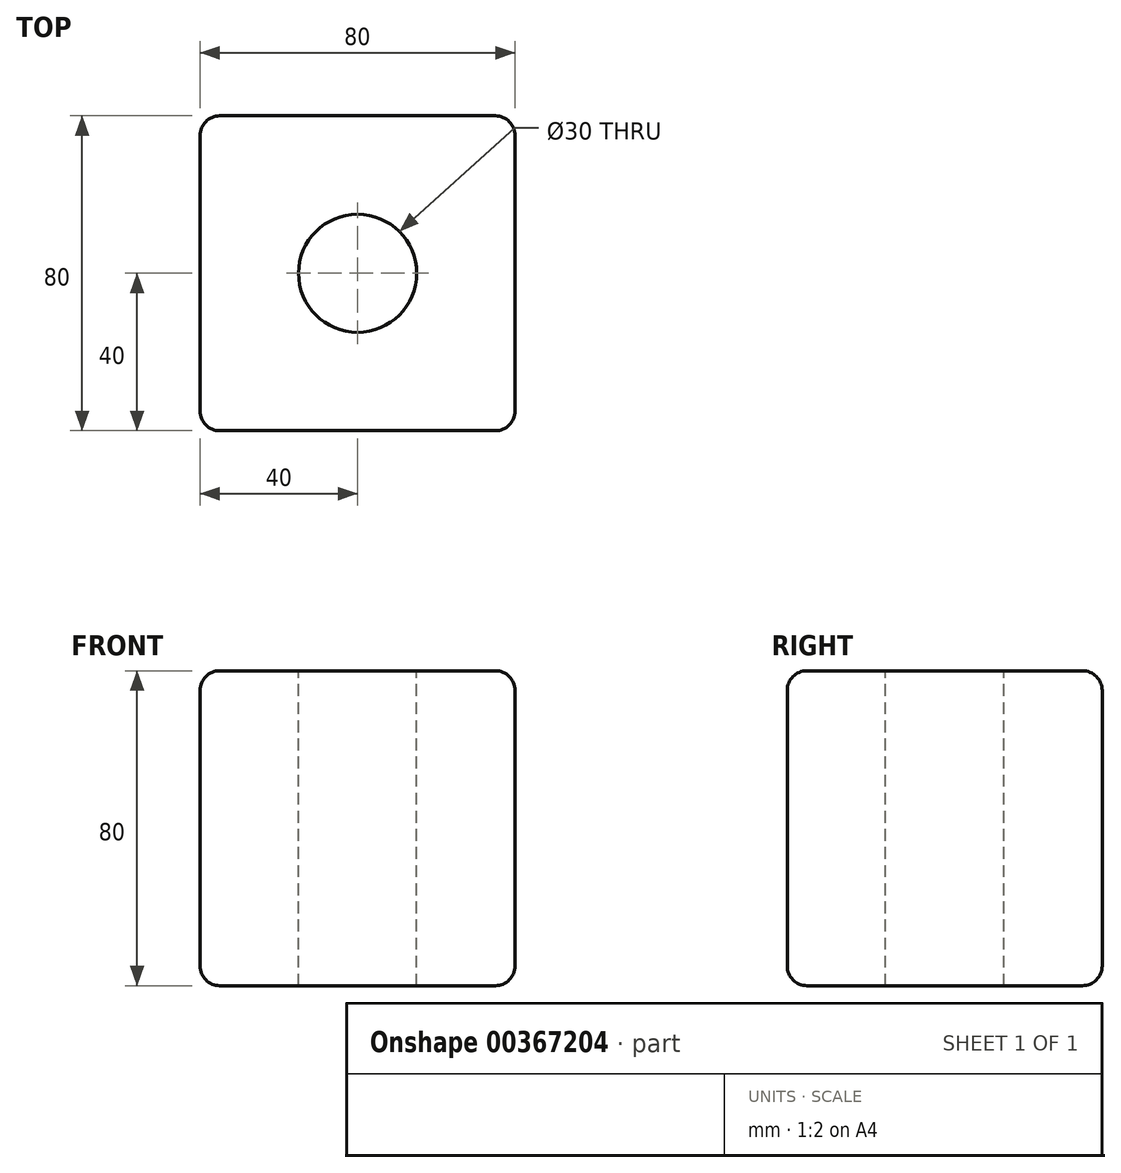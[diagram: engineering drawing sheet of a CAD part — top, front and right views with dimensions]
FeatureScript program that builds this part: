
annotation { "Feature Type Name" : "Feature", "Feature Type Description" : "" }
export const myFeature = defineFeature(function(context is Context, id is Id, definition is map)
    precondition{}
    {
        {
            var Q0;
            Q0=qCreatedBy(makeId("Top.planeOp"),FACE);
            var sketch = newSketch(context, id + "F0", { "sketchPlane" : qUnion([Q0])});
            skLineSegment(sketch, "E0.bottom", {"start": v(-40, 40) * mm, "end": v(40, 40) * mm});
            skLineSegment(sketch, "E0.top", {"start": v(-40, -40) * mm, "end": v(40, -40) * mm});
            skLineSegment(sketch, "E0.left", {"start": v(-40, 40) * mm, "end": v(-40, -40) * mm});
            skLineSegment(sketch, "E0.right", {"start": v(40, 40) * mm, "end": v(40, -40) * mm});
            skPoint(sketch, "E0.middle", {"position": v(0, 0) * mm});
            skSolve(sketch);
        }
        {
            var Q0;
            Q0=makeQuery(id+"F0.imprint","IMPRINT",FACE,{"disambiguationData":[TD([[makeQuery(id+"F0.imprint","IMPRINT",EDGE,{"derivedFrom":sQuery(id+"F0.wireOp",EDGE,"E0.bottom")}),-1.0]])]});
            extrude(context, id + "F1", {"entities" : qUnion([Q0]), "depth" : 80 * mm});
        }
        {
            var Q0;
            Q0=makeQuery(id+"F1.opExtrude","CAP_FACE",FACE,{"disambiguationData":[OSD([sQuery(id+"F0.wireOp",EDGE,"E0.bottom"),sQuery(id+"F0.wireOp",EDGE,"E0.top"),sQuery(id+"F0.wireOp",EDGE,"E0.left"),sQuery(id+"F0.wireOp",EDGE,"E0.right")])],"isStart":false});
            var sketch = newSketch(context, id + "F2", { "sketchPlane" : qUnion([Q0])});
            skCircle(sketch, "E1", {"center": v(0, 0) * mm, "radius": 15 * mm});
            skSolve(sketch);
        }
        {
            var Q0;
            Q0=makeQuery(id+"F2.imprint","IMPRINT",FACE,{"disambiguationData":[TD([[makeQuery(id+"F2.imprint","IMPRINT",EDGE,{"derivedFrom":sQuery(id+"F2.wireOp",EDGE,"E1")}),1.0]])]});
            extrude(context, id + "F3", {"entities" : qUnion([Q0]), "operationType" : NewBodyOperationType.REMOVE, "endBound" : BoundingType.THROUGH_ALL, "oppositeDirection" : true, "depth" : 25 * mm});
        }
        {
            var Q0;
            Q0=makeQuery(id+"F1.opExtrude","CAP_EDGE",EDGE,{"disambiguationData":[OSD([sQuery(id+"F0.wireOp",EDGE,"E0.left")])],"isStart":false});
            var Q1;
            Q1=makeQuery(id+"F1.opExtrude","CAP_EDGE",EDGE,{"disambiguationData":[OSD([sQuery(id+"F0.wireOp",EDGE,"E0.bottom")])],"isStart":false});
            var Q2;
            Q2=makeQuery(id+"F1.opExtrude","SWEPT_EDGE",EDGE,{"disambiguationData":[OSD([sQuery(id+"F0.wireOp",EDGE,"E0.top"),sQuery(id+"F0.wireOp",EDGE,"E0.right")])]});
            var Q3;
            Q3=makeQuery(id+"F1.opExtrude","CAP_EDGE",EDGE,{"disambiguationData":[OSD([sQuery(id+"F0.wireOp",EDGE,"E0.top")])],"isStart":false});
            var Q4;
            Q4=makeQuery(id+"F1.opExtrude","SWEPT_EDGE",EDGE,{"disambiguationData":[OSD([sQuery(id+"F0.wireOp",EDGE,"E0.bottom"),sQuery(id+"F0.wireOp",EDGE,"E0.left")])]});
            var Q5;
            Q5=makeQuery(id+"F1.opExtrude","CAP_EDGE",EDGE,{"disambiguationData":[OSD([sQuery(id+"F0.wireOp",EDGE,"E0.right")])],"isStart":false});
            var Q6;
            Q6=makeQuery(id+"F1.opExtrude","CAP_EDGE",EDGE,{"disambiguationData":[OSD([sQuery(id+"F0.wireOp",EDGE,"E0.left")])],"isStart":true});
            var Q7;
            Q7=makeQuery(id+"F1.opExtrude","SWEPT_EDGE",EDGE,{"disambiguationData":[OSD([sQuery(id+"F0.wireOp",EDGE,"E0.top"),sQuery(id+"F0.wireOp",EDGE,"E0.left")])]});
            var Q8;
            Q8=makeQuery(id+"F1.opExtrude","SWEPT_EDGE",EDGE,{"disambiguationData":[OSD([sQuery(id+"F0.wireOp",EDGE,"E0.bottom"),sQuery(id+"F0.wireOp",EDGE,"E0.right")])]});
            var Q9;
            Q9=makeQuery(id+"F1.opExtrude","SWEPT_FACE",FACE,{"disambiguationData":[OSD([sQuery(id+"F0.wireOp",EDGE,"E0.bottom")])]});
            var Q10;
            Q10=makeQuery(id+"F1.opExtrude","CAP_EDGE",EDGE,{"disambiguationData":[OSD([sQuery(id+"F0.wireOp",EDGE,"E0.right")])],"isStart":true});
            var Q11;
            Q11=makeQuery(id+"F1.opExtrude","CAP_EDGE",EDGE,{"disambiguationData":[OSD([sQuery(id+"F0.wireOp",EDGE,"E0.top")])],"isStart":true});
            fillet(context, id + "F4", {"entities" : qUnion([Q0, Q1, Q2, Q3, Q4, Q5, Q6, Q7, Q8, Q9, Q10, Q11]), "radius" : 5 * mm, "tangentPropagation" : true, "allowEdgeOverflow" : false});
        }
    });
